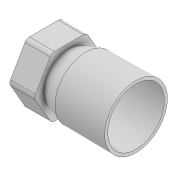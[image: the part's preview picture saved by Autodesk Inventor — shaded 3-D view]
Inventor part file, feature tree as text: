
AUTODESK INVENTOR PART (.ipt)
format: ipt  version: 2020 (Build 240168000, 168)  size: 188,416 bytes
history: native  units: mm
features: sketch x4, chamfer x3, revolve x2, extrude x2, pattern_circular x1, fillet x1, projected_geometry x1
ambient origin geometry x8: Origin, YZ Plane, XZ Plane, XY Plane, X Axis, Y Axis, Z Axis, Center Point
bodies: Solid1 (feature_tree)
feature tree (14):
  revolve  "Revolution1"  [1 undecoded]
  extrude  "Extrusion1"  Depth=12.45mm
  chamfer  "Chamfer1"  Distance=1.2mm
  pattern_circular  "Circular Pattern1"  [2 undecoded]
  chamfer  "Chamfer2"  Distance=10.0mm
  extrude  "Extrusion2"  TaperAngle=90.0deg  [1 undecoded]
  fillet  "Fillet1"  Radius=2.443461mm
  revolve  "Revolution2"  [1 undecoded]
  chamfer  "Chamfer3"  Distance=2.0mm Angle=45.0deg
  sketch  "Sketch1"  dims[d2=4.75mm d3=12.2mm]
  sketch  "Sketch2"  dims[d4=20.0mm d5=12.45mm]
  sketch  "Sketch3"  dims[d6=2.0mm]
  sketch  "Sketch4"  dims[d7=90.0deg d8=1.2mm d9=1.2mm d10=10.0mm d11=90.0deg d12=2.443461mm d13=10.0mm d14=0.0mm d15=4.0mm d16=2.0mm d17=45.0deg d18=50.0mm d19=360.0deg d21=0.7mm d22=2.0mm d23=45.0deg d24=30.961694mm d25=8.0mm d26=3.3mm d27=4.6mm d28=6.614426mm d29=10.0mm d30=0.0mm d31=2.0mm d32=24.0mm d33=5.6mm d34=0.3mm d35=90.0deg d36=1.0mm d37=2.0mm d38=45.0deg]
  projected_geometry  "Projected Loop1"
note: 5 required parameter values undecoded (feature->parameter linkage not recoverable at this tier; creation-order binding heuristic only, values carry confidence <= 0.55)